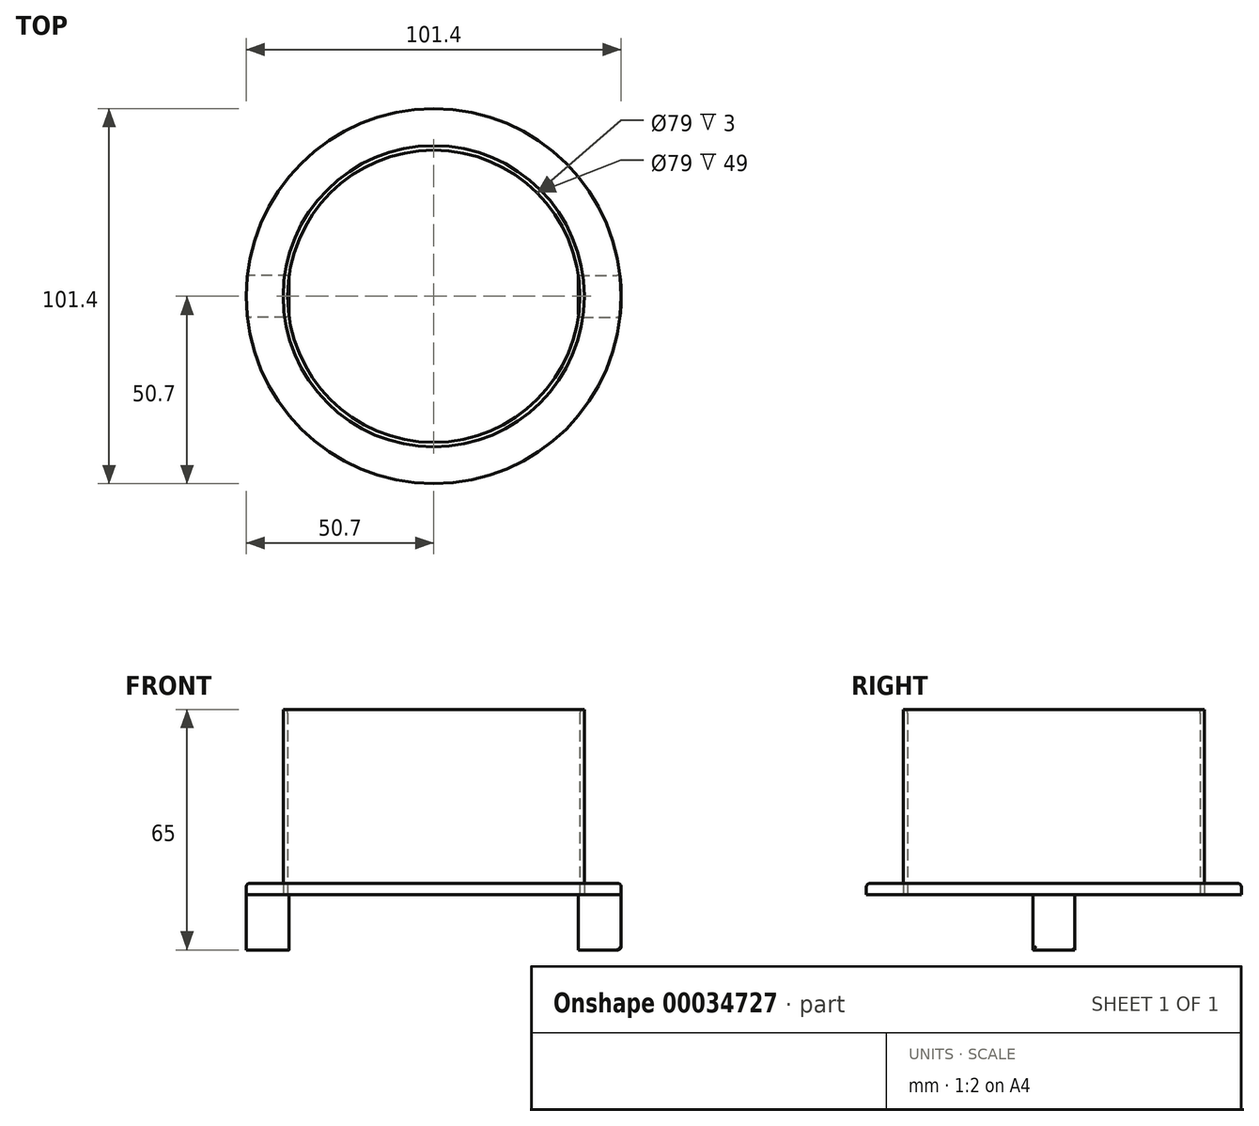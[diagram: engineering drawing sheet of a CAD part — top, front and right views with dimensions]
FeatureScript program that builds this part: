
annotation { "Feature Type Name" : "Feature", "Feature Type Description" : "" }
export const myFeature = defineFeature(function(context is Context, id is Id, definition is map)
    precondition{}
    {
        {
            var Q0;
            Q0=qCreatedBy(makeId("Top.planeOp"),FACE);
            var sketch = newSketch(context, id + "F0", { "sketchPlane" : qUnion([Q0])});
            skCircle(sketch, "E0", {"center": v(0, 0) * mm, "radius": 39.5 * mm});
            skCircle(sketch, "E1", {"center": v(0, 0) * mm, "radius": 40.7 * mm});
            skCircle(sketch, "E2", {"center": v(0, 0) * mm, "radius": 50.7 * mm});
            skLineSegment(sketch, "E3.bottom", {"start": v(39.1, 5.65) * mm, "end": v(50.38, 5.65) * mm});
            skLineSegment(sketch, "E3.top", {"start": v(39.1, -5.65) * mm, "end": v(50.38, -5.65) * mm});
            skLineSegment(sketch, "E3.left", {"start": v(39.1, 5.65) * mm, "end": v(39.1, -5.65) * mm});
            skLineSegment(sketch, "E3.right", {"start": v(50.38, 5.65) * mm, "end": v(50.38, -5.65) * mm});
            skLineSegment(sketch, "E4.MirrorCS", {"start": v(-39.1, 5.65) * mm, "end": v(-50.38, 5.65) * mm});
            skLineSegment(sketch, "E5.MirrorCS", {"start": v(-39.1, 5.65) * mm, "end": v(-39.1, -5.65) * mm});
            skLineSegment(sketch, "E6.MirrorCS", {"start": v(-39.1, -5.65) * mm, "end": v(-50.38, -5.65) * mm});
            skLineSegment(sketch, "E7.MirrorCS", {"start": v(-50.38, 5.65) * mm, "end": v(-50.38, -5.65) * mm});
            skSolve(sketch);
        }
        {
            var Q0;
            {var subQ0=sQuery(id+"F0.wireOp",EDGE,"rSKR8UN8-QKqV-kw3D-mcID-aLAz2qLQLhE0.bottom");var subQ1=sQuery(id+"F0.wireOp",EDGE,"E0");var subQ2=makeQuery(id+"F0.imprint","INTERSECT",VERTEX,{"disambiguationData":[OD(0.0)],"derivedFrom":[subQ1,subQ0]});Q0=makeQuery(id+"F0.imprint","IMPRINT",FACE,{"disambiguationData":[TD([[makeQuery(id+"F0.imprint","IMPRINT",EDGE,{"disambiguationData":[TD([[subQ2,1.0]])],"derivedFrom":subQ1}),-1.0]])]});}
            var Q1;
            {var subQ0=sQuery(id+"F0.wireOp",EDGE,"rSKR8UN8-QKqV-kw3D-mcID-aLAz2qLQLhE0.top");var subQ1=sQuery(id+"F0.wireOp",EDGE,"E0");var subQ2=makeQuery(id+"F0.imprint","INTERSECT",VERTEX,{"disambiguationData":[OD(0.0)],"derivedFrom":[subQ1,subQ0]});Q1=makeQuery(id+"F0.imprint","IMPRINT",FACE,{"disambiguationData":[TD([[makeQuery(id+"F0.imprint","IMPRINT",EDGE,{"disambiguationData":[TD([[subQ2,-1.0]])],"derivedFrom":subQ1}),-1.0]])]});}
            var Q2;
            {var subQ5=sQuery(id+"F0.wireOp",EDGE,"rSKR8UN8-QKqV-kw3D-mcID-aLAz2qLQLhE0.right");Q2=makeQuery(id+"F0.imprint","IMPRINT",FACE,{"disambiguationData":[TD([[makeQuery(id+"F0.imprint","IMPRINT",EDGE,{"derivedFrom":subQ5}),1.0]])]});}
            var Q3;
            {var subQ0=sQuery(id+"F0.wireOp",EDGE,"rSKR8UN8-QKqV-kw3D-mcID-aLAz2qLQLhE0.right");Q3=makeQuery(id+"F0.imprint","IMPRINT",FACE,{"disambiguationData":[TD([[makeQuery(id+"F0.imprint","IMPRINT",EDGE,{"derivedFrom":subQ0}),-1.0]])]});}
            var Q4;
            {var subQ5=sQuery(id+"F0.wireOp",EDGE,"rSKR8UN8-QKqV-kw3D-mcID-aLAz2qLQLhE0.left");Q4=makeQuery(id+"F0.imprint","IMPRINT",FACE,{"disambiguationData":[TD([[makeQuery(id+"F0.imprint","IMPRINT",EDGE,{"derivedFrom":subQ5}),-1.0]])]});}
            var Q5;
            {var subQ0=sQuery(id+"F0.wireOp",EDGE,"rSKR8UN8-QKqV-kw3D-mcID-aLAz2qLQLhE0.left");Q5=makeQuery(id+"F0.imprint","IMPRINT",FACE,{"disambiguationData":[TD([[makeQuery(id+"F0.imprint","IMPRINT",EDGE,{"derivedFrom":subQ0}),1.0]])]});}
            extrude(context, id + "F1", {"entities" : qUnion([Q0, Q1, Q2, Q3, Q4, Q5]), "depth" : 50 * mm, "offsetDistance" : 25 * mm});
        }
        {
            var Q0;
            {var subQ1=sQuery(id+"F0.wireOp",EDGE,"E3.bottom");var subQ6=sQuery(id+"F0.wireOp",EDGE,"E1");var subQ7=makeQuery(id+"F0.imprint","INTERSECT",VERTEX,{"derivedFrom":[subQ6,subQ1]});Q0=makeQuery(id+"F0.imprint","IMPRINT",FACE,{"disambiguationData":[TD([[makeQuery(id+"F0.imprint","IMPRINT",EDGE,{"disambiguationData":[TD([[subQ7,1.0]])],"derivedFrom":subQ6}),1.0]])]});}
            var Q1;
            {var subQ5=sQuery(id+"F0.wireOp",EDGE,"E3.right");Q1=makeQuery(id+"F0.imprint","IMPRINT",FACE,{"disambiguationData":[TD([[makeQuery(id+"F0.imprint","IMPRINT",EDGE,{"derivedFrom":subQ5}),-1.0]])]});}
            var Q2;
            {var subQ0=sQuery(id+"F0.wireOp",EDGE,"E3.right");Q2=makeQuery(id+"F0.imprint","IMPRINT",FACE,{"disambiguationData":[TD([[makeQuery(id+"F0.imprint","IMPRINT",EDGE,{"derivedFrom":subQ0}),1.0]])]});}
            var Q3;
            {var subQ1=sQuery(id+"F0.wireOp",EDGE,"E4.MirrorCS");var subQ6=sQuery(id+"F0.wireOp",EDGE,"E1");var subQ8=makeQuery(id+"F0.imprint","INTERSECT",VERTEX,{"derivedFrom":[subQ6,subQ1]});Q3=makeQuery(id+"F0.imprint","IMPRINT",FACE,{"disambiguationData":[TD([[makeQuery(id+"F0.imprint","IMPRINT",EDGE,{"disambiguationData":[TD([[subQ8,-1.0]])],"derivedFrom":subQ6}),1.0]])]});}
            var Q4;
            {var subQ5=sQuery(id+"F0.wireOp",EDGE,"E7.MirrorCS");Q4=makeQuery(id+"F0.imprint","IMPRINT",FACE,{"disambiguationData":[TD([[makeQuery(id+"F0.imprint","IMPRINT",EDGE,{"derivedFrom":subQ5}),1.0]])]});}
            var Q5;
            {var subQ0=sQuery(id+"F0.wireOp",EDGE,"E7.MirrorCS");Q5=makeQuery(id+"F0.imprint","IMPRINT",FACE,{"disambiguationData":[TD([[makeQuery(id+"F0.imprint","IMPRINT",EDGE,{"derivedFrom":subQ0}),-1.0]])]});}
            var Q6;
            {var subQ0=sQuery(id+"F0.wireOp",EDGE,"E5.MirrorCS");Q6=makeQuery(id+"F0.imprint","IMPRINT",FACE,{"disambiguationData":[TD([[makeQuery(id+"F0.imprint","IMPRINT",EDGE,{"derivedFrom":subQ0}),-1.0]])]});}
            var Q7;
            {var subQ0=sQuery(id+"F0.wireOp",EDGE,"E3.left");Q7=makeQuery(id+"F0.imprint","IMPRINT",FACE,{"disambiguationData":[TD([[makeQuery(id+"F0.imprint","IMPRINT",EDGE,{"derivedFrom":subQ0}),1.0]])]});}
            extrude(context, id + "F2", {"entities" : qUnion([Q0, Q1, Q2, Q3, Q4, Q5, Q6, Q7]), "oppositeDirection" : true, "depth" : 15 * mm, "offsetDistance" : 25 * mm});
        }
        {
            var Q0;
            {var subQ0=sQuery(id+"F0.wireOp",EDGE,"E4.MirrorCS");var subQ1=sQuery(id+"F0.wireOp",EDGE,"E1");var subQ2=makeQuery(id+"F0.imprint","INTERSECT",VERTEX,{"derivedFrom":[subQ1,subQ0]});Q0=makeQuery(id+"F0.imprint","IMPRINT",FACE,{"disambiguationData":[TD([[makeQuery(id+"F0.imprint","IMPRINT",EDGE,{"disambiguationData":[TD([[subQ2,1.0]])],"derivedFrom":subQ1}),-1.0]])]});}
            var Q1;
            {var subQ0=sQuery(id+"F0.wireOp",EDGE,"E6.MirrorCS");var subQ1=sQuery(id+"F0.wireOp",EDGE,"E1");var subQ2=makeQuery(id+"F0.imprint","INTERSECT",VERTEX,{"derivedFrom":[subQ1,subQ0]});Q1=makeQuery(id+"F0.imprint","IMPRINT",FACE,{"disambiguationData":[TD([[makeQuery(id+"F0.imprint","IMPRINT",EDGE,{"disambiguationData":[TD([[subQ2,-1.0]])],"derivedFrom":subQ1}),-1.0]])]});}
            var Q2;
            {var subQ5=sQuery(id+"F0.wireOp",EDGE,"E3.right");Q2=makeQuery(id+"F0.imprint","IMPRINT",FACE,{"disambiguationData":[TD([[makeQuery(id+"F0.imprint","IMPRINT",EDGE,{"derivedFrom":subQ5}),-1.0]])]});}
            var Q3;
            {var subQ5=sQuery(id+"F0.wireOp",EDGE,"E7.MirrorCS");Q3=makeQuery(id+"F0.imprint","IMPRINT",FACE,{"disambiguationData":[TD([[makeQuery(id+"F0.imprint","IMPRINT",EDGE,{"derivedFrom":subQ5}),1.0]])]});}
            var Q4;
            {var subQ0=sQuery(id+"F0.wireOp",EDGE,"E7.MirrorCS");Q4=makeQuery(id+"F0.imprint","IMPRINT",FACE,{"disambiguationData":[TD([[makeQuery(id+"F0.imprint","IMPRINT",EDGE,{"derivedFrom":subQ0}),-1.0]])]});}
            var Q5;
            {var subQ3=sQuery(id+"F0.wireOp",EDGE,"E4.MirrorCS");var subQ5=sQuery(id+"F0.wireOp",EDGE,"E1");var subQ6=makeQuery(id+"F0.imprint","INTERSECT",VERTEX,{"derivedFrom":[subQ5,subQ3]});Q5=makeQuery(id+"F0.imprint","IMPRINT",FACE,{"disambiguationData":[TD([[makeQuery(id+"F0.imprint","IMPRINT",EDGE,{"disambiguationData":[TD([[subQ6,1.0]])],"derivedFrom":subQ5}),1.0]])]});}
            var Q6;
            {var subQ1=sQuery(id+"F0.wireOp",EDGE,"E3.bottom");var subQ6=sQuery(id+"F0.wireOp",EDGE,"E1");var subQ7=makeQuery(id+"F0.imprint","INTERSECT",VERTEX,{"derivedFrom":[subQ6,subQ1]});Q6=makeQuery(id+"F0.imprint","IMPRINT",FACE,{"disambiguationData":[TD([[makeQuery(id+"F0.imprint","IMPRINT",EDGE,{"disambiguationData":[TD([[subQ7,1.0]])],"derivedFrom":subQ6}),1.0]])]});}
            var Q7;
            {var subQ3=sQuery(id+"F0.wireOp",EDGE,"E6.MirrorCS");var subQ5=sQuery(id+"F0.wireOp",EDGE,"E1");var subQ6=makeQuery(id+"F0.imprint","INTERSECT",VERTEX,{"derivedFrom":[subQ5,subQ3]});Q7=makeQuery(id+"F0.imprint","IMPRINT",FACE,{"disambiguationData":[TD([[makeQuery(id+"F0.imprint","IMPRINT",EDGE,{"disambiguationData":[TD([[subQ6,-1.0]])],"derivedFrom":subQ5}),1.0]])]});}
            var Q8;
            {var subQ1=sQuery(id+"F0.wireOp",EDGE,"E4.MirrorCS");var subQ6=sQuery(id+"F0.wireOp",EDGE,"E1");var subQ8=makeQuery(id+"F0.imprint","INTERSECT",VERTEX,{"derivedFrom":[subQ6,subQ1]});Q8=makeQuery(id+"F0.imprint","IMPRINT",FACE,{"disambiguationData":[TD([[makeQuery(id+"F0.imprint","IMPRINT",EDGE,{"disambiguationData":[TD([[subQ8,-1.0]])],"derivedFrom":subQ6}),1.0]])]});}
            var Q9;
            {var subQ0=sQuery(id+"F0.wireOp",EDGE,"E3.right");Q9=makeQuery(id+"F0.imprint","IMPRINT",FACE,{"disambiguationData":[TD([[makeQuery(id+"F0.imprint","IMPRINT",EDGE,{"derivedFrom":subQ0}),1.0]])]});}
            extrude(context, id + "F3", {"entities" : qUnion([Q0, Q1, Q2, Q3, Q4, Q5, Q6, Q7, Q8, Q9]), "depth" : 3 * mm, "offsetDistance" : 25 * mm});
        }
        {
            var Q0;
            Q0=makeQuery(id+"F3.opExtrude","CAP_EDGE",EDGE,{"disambiguationData":[OSD([sQuery(id+"F0.wireOp",EDGE,"E2")])],"isStart":false});
            var Q1;
            Q1=makeQuery(id+"F2.opExtrude","SWEPT_EDGE",EDGE,{"disambiguationData":[OSD([sQuery(id+"F0.wireOp",EDGE,"E0"),sQuery(id+"F0.wireOp",EDGE,"E5.MirrorCS"),sQuery(id+"F0.wireOp",EDGE,"E6.MirrorCS")])]});
            var Q2;
            Q2=makeQuery(id+"F2.opExtrude","SWEPT_EDGE",EDGE,{"disambiguationData":[OSD([sQuery(id+"F0.wireOp",EDGE,"E0"),sQuery(id+"F0.wireOp",EDGE,"E3.top"),sQuery(id+"F0.wireOp",EDGE,"E3.left")])]});
            var Q3;
            Q3=makeQuery(id+"F2.opExtrude","SWEPT_EDGE",EDGE,{"disambiguationData":[OSD([sQuery(id+"F0.wireOp",EDGE,"E2"),sQuery(id+"F0.wireOp",EDGE,"E6.MirrorCS"),sQuery(id+"F0.wireOp",EDGE,"E7.MirrorCS")])]});
            var Q4;
            Q4=makeQuery(id+"F2.opExtrude","SWEPT_EDGE",EDGE,{"disambiguationData":[OSD([sQuery(id+"F0.wireOp",EDGE,"E2"),sQuery(id+"F0.wireOp",EDGE,"E4.MirrorCS"),sQuery(id+"F0.wireOp",EDGE,"E7.MirrorCS")])]});
            var Q5;
            Q5=makeQuery(id+"F1.opExtrude","CAP_EDGE",EDGE,{"disambiguationData":[OSD([sQuery(id+"F0.wireOp",EDGE,"E0")])],"isStart":false});
            var Q6;
            Q6=makeQuery(id+"F2.opExtrude","SWEPT_EDGE",EDGE,{"disambiguationData":[OSD([sQuery(id+"F0.wireOp",EDGE,"E2"),sQuery(id+"F0.wireOp",EDGE,"E3.bottom"),sQuery(id+"F0.wireOp",EDGE,"E3.right")])]});
            var Q7;
            {var subQ0=sQuery(id+"F0.wireOp",EDGE,"E3.right");var subQ1=sQuery(id+"F0.wireOp",EDGE,"E2");Q7=makeQuery(id+"F2.opExtrude","CAP_EDGE",EDGE,{"disambiguationData":[OSD([subQ1]),TDD([makeQuery(id+"F0.imprint","IMPRINT",EDGE,{"disambiguationData":[TD([[makeQuery(id+"F0.imprint","INTERSECT",VERTEX,{"derivedFrom":[subQ1,sQuery(id+"F0.wireOp",EDGE,"E3.bottom"),subQ0]}),1.0]])],"derivedFrom":subQ1})])],"isStart":false});}
            var Q8;
            Q8=makeQuery(id+"F2.opExtrude","CAP_EDGE",EDGE,{"disambiguationData":[OSD([sQuery(id+"F0.wireOp",EDGE,"E3.bottom")])],"isStart":false});
            var Q9;
            Q9=makeQuery(id+"F2.opExtrude","SWEPT_EDGE",EDGE,{"disambiguationData":[OSD([sQuery(id+"F0.wireOp",EDGE,"E2"),sQuery(id+"F0.wireOp",EDGE,"E3.top"),sQuery(id+"F0.wireOp",EDGE,"E3.right")])]});
            fillet(context, id + "F4", {"entities" : qUnion([Q0, Q1, Q2, Q3, Q4, Q5, Q6, Q7, Q8, Q9]), "radius" : 1 * mm, "tangentPropagation" : true, "allowEdgeOverflow" : false});
        }
    });
